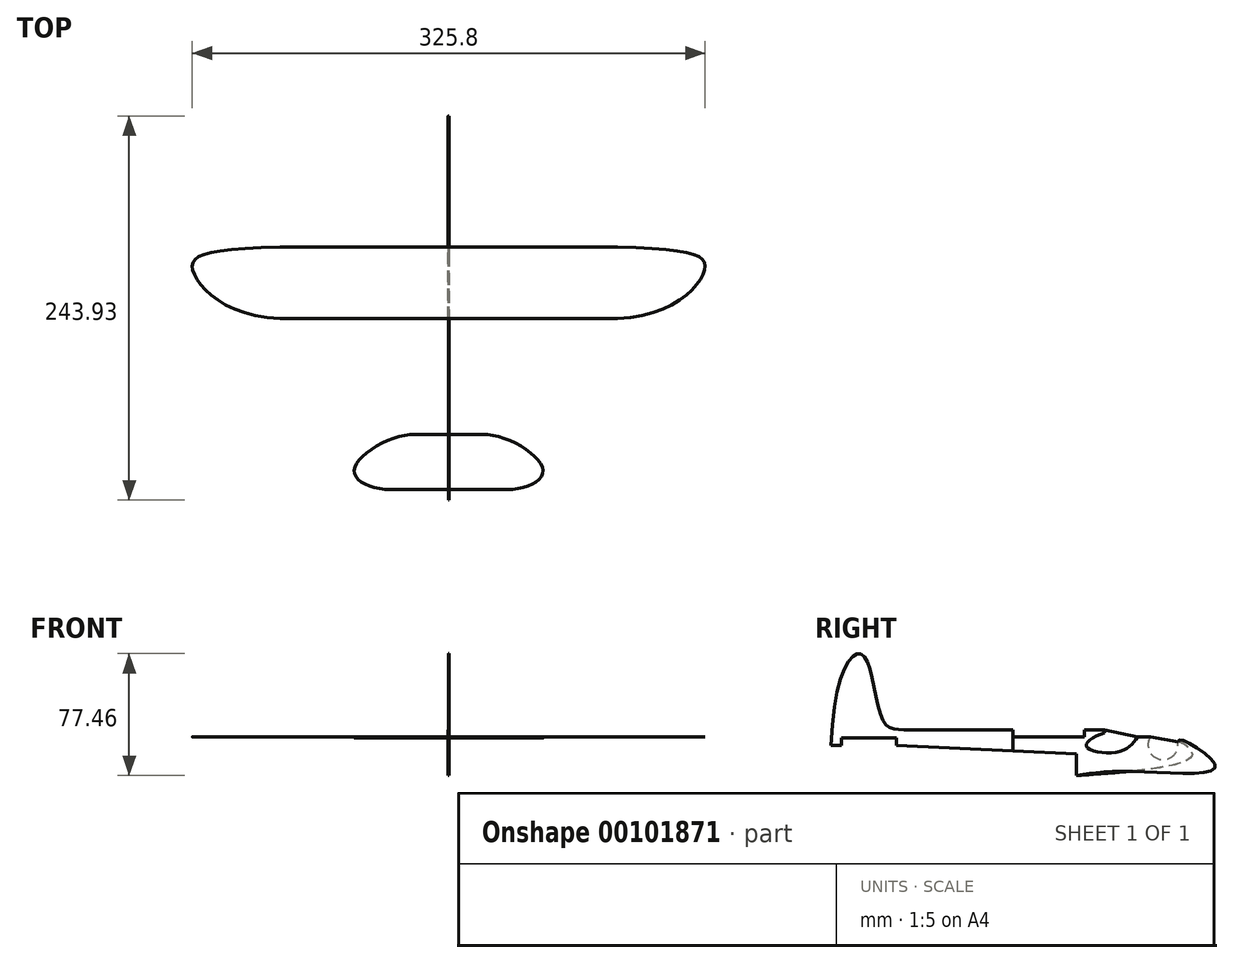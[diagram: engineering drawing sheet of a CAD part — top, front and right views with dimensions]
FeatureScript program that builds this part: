
annotation { "Feature Type Name" : "Feature", "Feature Type Description" : "" }
export const myFeature = defineFeature(function(context is Context, id is Id, definition is map)
    precondition{}
    {
        {
            assignVariable(context, id + "F0", {"name" : "FW", "anyValue" : 3 / 16});
        }
        {
            var Q0;
            Q0=qCreatedBy(makeId("Right.planeOp"),FACE);
            var sketch = newSketch(context, id + "F1", { "sketchPlane" : qUnion([Q0])});
            skLineSegment(sketch, "E0", {"start": v(0, 0) * mm, "end": v(-114.17, 5.42) * mm});
            skLineSegment(sketch, "E1", {"start": v(-114.17, 5.42) * mm, "end": v(-114.17, 10.18) * mm});
            skLineSegment(sketch, "E2", {"start": v(-114.17, 10.18) * mm, "end": v(-149.1, 10.18) * mm});
            skLineSegment(sketch, "E3", {"start": v(-149.1, 10.18) * mm, "end": v(-149.1, 5.42) * mm});
            skLineSegment(sketch, "E4", {"start": v(-149.1, 5.42) * mm, "end": v(-155.66, 5.42) * mm});
            skFitSpline(sketch, "E5", {"points": [v(-155.66, 5.42) * mm, v(-134.84, 62) * mm, v(-122.2, 20.29) * mm, v(-109.55, 15.2) * mm], "startDerivative": vector(8.27, 316.76) * mm, "endDerivative": vector(80.3, -8.3) * mm});
            skLineSegment(sketch, "E6", {"start": v(-109.55, 15.2) * mm, "end": v(-40.3, 15.2) * mm});
            skLineSegment(sketch, "E7", {"start": v(-40.3, 15.2) * mm, "end": v(-40.3, 10.66) * mm});
            skLineSegment(sketch, "E8", {"start": v(-40.3, 10.66) * mm, "end": v(5.19, 10.66) * mm});
            skLineSegment(sketch, "E9", {"start": v(5.19, 10.66) * mm, "end": v(5.19, 15.2) * mm});
            skLineSegment(sketch, "E10", {"start": v(5.19, 15.2) * mm, "end": v(17.83, 15.2) * mm});
            skLineSegment(sketch, "E11", {"start": v(17.83, 15.2) * mm, "end": v(38.97, 10.85) * mm});
            skLineSegment(sketch, "E12", {"start": v(38.97, 10.85) * mm, "end": v(47.08, 10.85) * mm});
            skArc(sketch, "E13", {"start": v(47.08, 10.85) * mm, "mid": v(52.94, -3.5) * mm, "end": v(64.62, 6.68) * mm});
            skFitSpline(sketch, "E14", {"points": [v(64.62, 6.68) * mm, v(65.8, 7.53) * mm, v(73.6, 0) * mm, v(0, -13.74) * mm], "startDerivative": vector(7.42, 14.93) * mm, "endDerivative": vector(-168.94, -11.9) * mm});
            skLineSegment(sketch, "E15", {"start": v(0, 0) * mm, "end": v(0, -13.74) * mm});
            skSolve(sketch);
        }
        {
            var Q0;
            Q0 = qSketchRegion(id + "F1", true);
            extrude(context, id + "F2", {"entities" : qUnion([Q0]), "depth" : (getVariable(context, 'FW')) * mm / 2, "hasSecondDirection" : true, "secondDirectionOppositeDirection" : true, "secondDirectionDepth" : (getVariable(context, 'FW') / 2) * mm});
        }
        {
            var Q0;
            Q0=makeQuery(id+"F2.opExtrude","CAP_FACE",FACE,{"disambiguationData":[OSD([sQuery(id+"F1.wireOp",EDGE,"E0"),sQuery(id+"F1.wireOp",EDGE,"E1"),sQuery(id+"F1.wireOp",EDGE,"E2"),sQuery(id+"F1.wireOp",EDGE,"E3"),sQuery(id+"F1.wireOp",EDGE,"E4"),sQuery(id+"F1.wireOp",EDGE,"E5"),sQuery(id+"F1.wireOp",EDGE,"E6"),sQuery(id+"F1.wireOp",EDGE,"E7"),sQuery(id+"F1.wireOp",EDGE,"E8"),sQuery(id+"F1.wireOp",EDGE,"E9"),sQuery(id+"F1.wireOp",EDGE,"E10"),sQuery(id+"F1.wireOp",EDGE,"E11"),sQuery(id+"F1.wireOp",EDGE,"E12"),sQuery(id+"F1.wireOp",EDGE,"E13"),sQuery(id+"F1.wireOp",EDGE,"E14"),sQuery(id+"F1.wireOp",EDGE,"E15")])],"isStart":false});
            var sketch = newSketch(context, id + "F3", { "sketchPlane" : qUnion([Q0])});
            skLineSegment(sketch, "E16", {"start": v(-40.3, 10.66) * mm, "end": v(-40.3, 1.91) * mm});
            skLineSegment(sketch, "E17.1", {"start": v(-40.3, 10.66) * mm, "end": v(5.19, 10.66) * mm});
            skLineSegment(sketch, "E17.2", {"start": v(5.19, 10.66) * mm, "end": v(5.19, 15.2) * mm});
            skLineSegment(sketch, "E17.3", {"start": v(5.19, 15.2) * mm, "end": v(17.83, 15.2) * mm});
            skLineSegment(sketch, "E17.5", {"start": v(38.97, 10.85) * mm, "end": v(47.08, 10.85) * mm});
            skFitSpline(sketch, "E17.7", {"points": [v(64.62, 6.68) * mm, v(64.85, 7.14) * mm, v(65.7, 8.84) * mm, v(88.24, -7.53) * mm, v(37.06, -11.13) * mm, v(0, -13.74) * mm]});
            skLineSegment(sketch, "E17.8", {"start": v(0, 0) * mm, "end": v(0, -13.74) * mm});
            skLineSegment(sketch, "E17.9", {"start": v(0, 0) * mm, "end": v(-40.3, 1.91) * mm});
            skPoint(sketch, "E18.orphan", {"position": v(-114.17, 5.42) * mm});
            skLineSegment(sketch, "E19", {"start": v(17.83, 15.2) * mm, "end": v(17.83, 13.35) * mm});
            skFitSpline(sketch, "E20", {"points": [v(17.83, 13.35) * mm, v(6.42, 4.81) * mm, v(27.05, 1.36) * mm, v(38.97, 10.85) * mm], "startDerivative": vector(-56.55, -16.49) * mm, "endDerivative": vector(26.74, 39.32) * mm});
            skLineSegment(sketch, "E21", {"start": v(47.08, 10.85) * mm, "end": v(65.88, 7.51) * mm});
            skSolve(sketch);
        }
        {
            var Q0;
            Q0 = qSketchRegion(id + "F3", true);
            extrude(context, id + "F4", {"entities" : qUnion([Q0]), "depth" : (getVariable(context, 'FW')) * mm});
        }
        {
            var Q0;
            Q0=makeQuery(id+"F4.opExtrude","SWEPT_BODY",BODY,{"disambiguationData":[OSD([sQuery(id+"F3.wireOp",EDGE,"E16"),sQuery(id+"F3.wireOp",EDGE,"E17.1"),sQuery(id+"F3.wireOp",EDGE,"E17.2"),sQuery(id+"F3.wireOp",EDGE,"E17.3"),sQuery(id+"F3.wireOp",EDGE,"E17.4"),sQuery(id+"F3.wireOp",EDGE,"E17.5"),sQuery(id+"F3.wireOp",EDGE,"E17.7"),sQuery(id+"F3.wireOp",EDGE,"E17.8"),sQuery(id+"F3.wireOp",EDGE,"E17.9"),sQuery(id+"F3.wireOp",EDGE,"bb20NDlU-s5jj-zeuj-KPjS-PQqiAS5GFbUK")])]});
            var Q1;
            Q1=qCreatedBy(makeId("Right.planeOp"),FACE);
            mirror(context, id + "F5", {"entities" : qUnion([Q0]), "mirrorPlane" : qUnion([Q1])});
        }
        {
            var Q0;
            Q0=makeQuery(id+"F2.opExtrude","SWEPT_FACE",FACE,{"disambiguationData":[OSD([sQuery(id+"F1.wireOp",EDGE,"E8")])]});
            var sketch = newSketch(context, id + "F6", { "sketchPlane" : qUnion([Q0])});
            skPoint(sketch, "E22.oppositeSnap0", {"position": v(0, -40.3) * mm});
            skLineSegment(sketch, "E22.bottom", {"start": v(0, 5.19) * mm, "end": v(107.14, 5.19) * mm});
            skLineSegment(sketch, "E22.top", {"start": v(0, -40.3) * mm, "end": v(107.14, -40.3) * mm});
            skFitSpline(sketch, "E23", {"points": [v(107.14, 5.19) * mm, v(162.4, -10.12) * mm, v(107.14, -40.3) * mm], "startDerivative": vector(293.03, -9.18) * mm, "endDerivative": vector(-195.6, -4.23) * mm});
            skLineSegment(sketch, "E24.MirrorCS", {"start": v(0, 5.19) * mm, "end": v(-107.14, 5.19) * mm});
            skFitSpline(sketch, "E25.MirrorCS", {"points": [v(-107.14, 5.19) * mm, v(-162.4, -10.12) * mm, v(-107.14, -40.3) * mm], "startDerivative": vector(-293.03, -9.18) * mm, "endDerivative": vector(195.6, -4.23) * mm});
            skLineSegment(sketch, "E26.MirrorCS", {"start": v(0, -40.3) * mm, "end": v(-107.14, -40.3) * mm});
            skSolve(sketch);
        }
        {
            var Q0;
            Q0 = qSketchRegion(id + "F6", true);
            extrude(context, id + "F7", {"entities" : qUnion([Q0]), "depth" : (getVariable(context, 'FW')) * mm});
        }
        {
            var Q0;
            Q0=makeQuery(id+"F2.opExtrude","SWEPT_FACE",FACE,{"disambiguationData":[OSD([sQuery(id+"F1.wireOp",EDGE,"E2")])]});
            var sketch = newSketch(context, id + "F8", { "sketchPlane" : qUnion([Q0])});
            skLineSegment(sketch, "E27.bottom", {"start": v(0, 149.1) * mm, "end": v(36.84, 149.1) * mm});
            skLineSegment(sketch, "E27.top", {"start": v(0, 114.17) * mm, "end": v(24.62, 114.17) * mm});
            skFitSpline(sketch, "E28", {"points": [v(36.84, 149.1) * mm, v(59.94, 136.44) * mm, v(24.62, 114.17) * mm], "startDerivative": vector(84.82, -1.77) * mm, "endDerivative": vector(-76.65, -4.84) * mm});
            skLineSegment(sketch, "E29.MirrorCS", {"start": v(0, 114.17) * mm, "end": v(-24.62, 114.17) * mm});
            skFitSpline(sketch, "E30.MirrorCS", {"points": [v(-36.84, 149.1) * mm, v(-59.94, 136.44) * mm, v(-24.62, 114.17) * mm], "startDerivative": vector(-84.82, -1.77) * mm, "endDerivative": vector(76.65, -4.84) * mm});
            skLineSegment(sketch, "E31.MirrorCS", {"start": v(0, 149.1) * mm, "end": v(-36.84, 149.1) * mm});
            skSolve(sketch);
        }
        {
            var Q0;
            {var subQ2=sQuery(id+"F8.wireOp",EDGE,"E30.MirrorCS");Q0=makeQuery(id+"F8.imprint","IMPRINT",FACE,{"disambiguationData":[TD([[makeQuery(id+"F8.imprint","IMPRINT",EDGE,{"derivedFrom":subQ2}),1.0]])]});}
            var Q1;
            {var subQ2=sQuery(id+"F8.wireOp",EDGE,"E28");Q1=makeQuery(id+"F8.imprint","IMPRINT",FACE,{"disambiguationData":[TD([[makeQuery(id+"F8.imprint","IMPRINT",EDGE,{"derivedFrom":subQ2}),-1.0]])]});}
            var Q2;
            {var subQ1=sQuery(id+"F1.wireOp",EDGE,"E2");var subQ2=makeQuery(id+"F2.opExtrude","CAP_EDGE",EDGE,{"disambiguationData":[OSD([subQ1])],"isStart":true});Q2=makeQuery(id+"F8.imprint","IMPRINT",FACE,{"disambiguationData":[TD([[makeQuery(id+"F8.imprint","IMPRINT",EDGE,{"derivedFrom":subQ2}),-1.0]])]});}
            extrude(context, id + "F9", {"entities" : qUnion([Q0, Q1, Q2]), "depth" : (getVariable(context, 'FW')) * mm});
        }
    });
